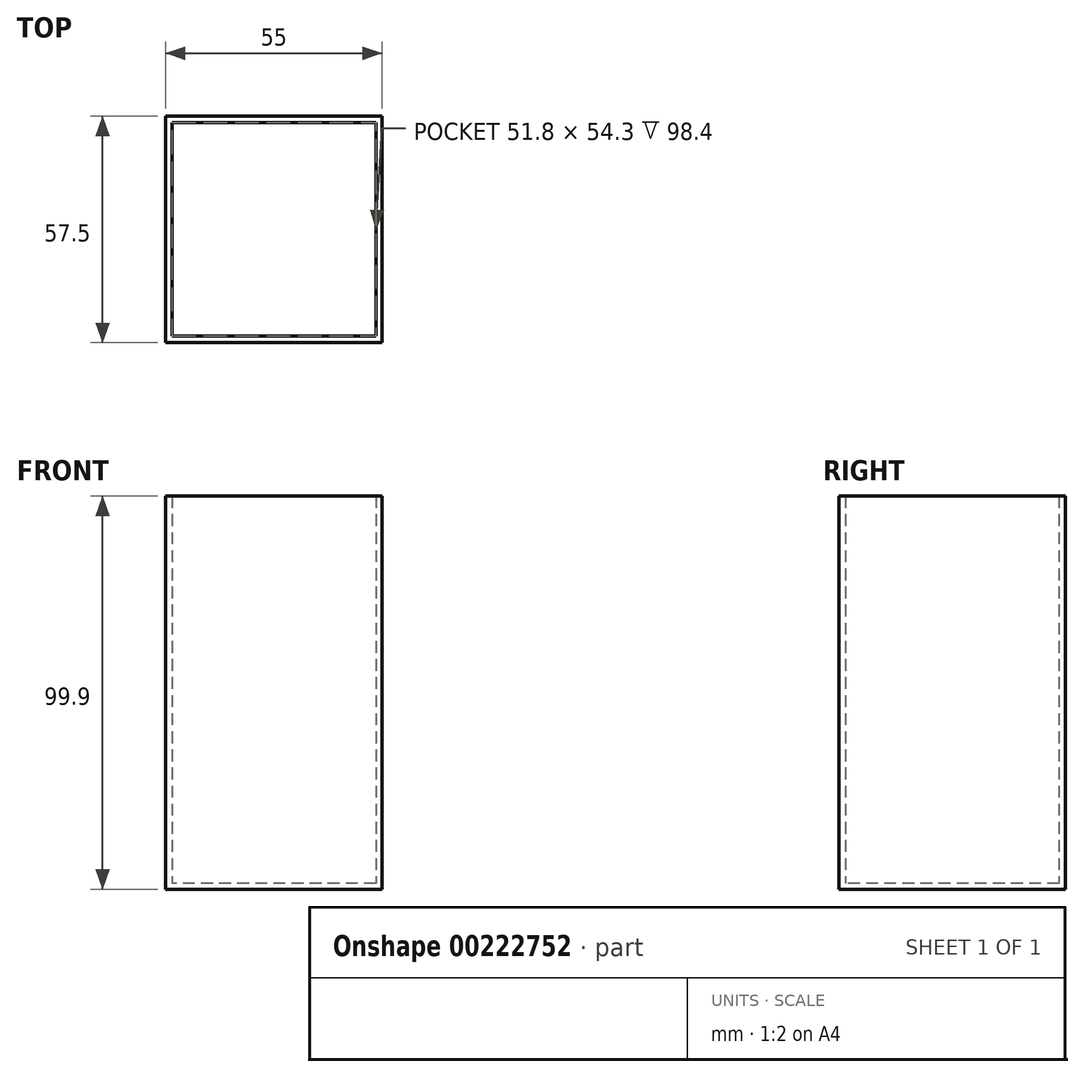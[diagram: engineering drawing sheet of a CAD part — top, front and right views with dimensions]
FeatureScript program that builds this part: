
annotation { "Feature Type Name" : "Feature", "Feature Type Description" : "" }
export const myFeature = defineFeature(function(context is Context, id is Id, definition is map)
    precondition{}
    {
        {
            var Q0;
            Q0=qCreatedBy(makeId("Top.planeOp"),FACE);
            var sketch = newSketch(context, id + "F0", { "sketchPlane" : qUnion([Q0])});
            skLineSegment(sketch, "E0.bottom", {"start": v(-26.03, 26.98) * mm, "end": v(28.97, 26.98) * mm});
            skLineSegment(sketch, "E0.top", {"start": v(-26.03, -30.52) * mm, "end": v(28.97, -30.52) * mm});
            skLineSegment(sketch, "E0.left", {"start": v(-26.03, 26.98) * mm, "end": v(-26.03, -30.52) * mm});
            skLineSegment(sketch, "E0.right", {"start": v(28.97, 26.98) * mm, "end": v(28.97, -30.52) * mm});
            skSolve(sketch);
        }
        {
            var Q0;
            Q0=makeQuery(id+"F0.imprint","IMPRINT",FACE,{"disambiguationData":[TD([[makeQuery(id+"F0.imprint","IMPRINT",EDGE,{"derivedFrom":sQuery(id+"F0.wireOp",EDGE,"E0.bottom")}),-1.0]])]});
            extrude(context, id + "F1", {"entities" : qUnion([Q0]), "depth" : 1.5 * mm});
        }
        {
            var Q0;
            Q0=makeQuery(id+"F1.opExtrude","CAP_FACE",FACE,{"disambiguationData":[OSD([sQuery(id+"F0.wireOp",EDGE,"E0.bottom"),sQuery(id+"F0.wireOp",EDGE,"E0.top"),sQuery(id+"F0.wireOp",EDGE,"E0.left"),sQuery(id+"F0.wireOp",EDGE,"E0.right")])],"isStart":false});
            var sketch = newSketch(context, id + "F2", { "sketchPlane" : qUnion([Q0])});
            skLineSegment(sketch, "E1.0", {"start": v(-24.43, 25.38) * mm, "end": v(-24.43, -28.92) * mm});
            skLineSegment(sketch, "E1.1", {"start": v(27.37, 25.38) * mm, "end": v(-24.43, 25.38) * mm});
            skLineSegment(sketch, "E1.2", {"start": v(27.37, -28.92) * mm, "end": v(27.37, 25.38) * mm});
            skLineSegment(sketch, "E1.3", {"start": v(-24.43, -28.92) * mm, "end": v(27.37, -28.92) * mm});
            skSolve(sketch);
        }
        {
            var Q0;
            Q0=makeQuery(id+"F2.imprint","IMPRINT",FACE,{"disambiguationData":[TD([[makeQuery(id+"F2.imprint","IMPRINT",EDGE,{"derivedFrom":sQuery(id+"F2.wireOp",EDGE,"E1.0")}),-1.0]])]});
            extrude(context, id + "F3", {"entities" : qUnion([Q0]), "operationType" : NewBodyOperationType.ADD, "depth" : 98.4 * mm});
        }
    });
